# Revit family: 2060533 Sylvania Lighting Fixture ASCENT100 II ARCH 1900 3K DALI EMG 120
name_source: partatom
category: Lighting Fixtures
revit_build: Autodesk Revit 2016 (Build: 20150220_1215(x64)
units: mm (PartAtom-declared; Revit-internal decimal feet)

## family parameters
Cut with Voids When Loaded = No
Host = Face
Light Source = Yes
OmniClass Number = 23.80.70.11.17
OmniClass Title = Specialized Lighting by Location or Use
Part Type = Normal
Room Calculation Point = No
Round Connector Dimension = Use Diameter
Shared = No

## types (2) — shared parameters
Aperture_SYL = 120 mm
Assembly Code = D5020200
AssetType = Fixed
Color Filter = 16777215
CutoutDiameter_SYL = 137 mm  [stored 0.449475 ft]
Description = Direct LED retro fit for original LED 100 Arch (120) single CFL lamp offering Matching lumen levels and improved light distribution of original LED 100 CFL lamp equivalents Typically half the power consumption compared to CFL Up to 104lm/W 120mm aperture Architectural reflector accepts range of glass accessories from existing LED 100 Arch 120 offering HE, HO and VHO versions equivalent of single 1 x 13W, 1 x 18W, 1 x 26W Additional VVHO versions which offer the performance circa 2 x 26W equivalent
Diameter_SYL = 150 mm
DiffuserRadius_SYL = 53 mm  [stored 0.173885 ft]
Dimming Lamp Color Temperature Shift = <None>
DocumentationLiterature = http://www.sylvania-lighting.com
DurationUnit = hours
ElectricShockClassification = Class II
Emit Shape Visible in Rendering = No
Emit from Circle Diameter = 106 mm  [stored 0.347769 ft]
ExpectedLife = 50000
Height_SYL = 94 mm  [stored 0.308399 ft]
IfcExportAs = IfcLightFixtureType
IfcExportType = IfcLightFixtureType
ImpactProtectionIndex = IK02
IngressProtection = IP40
Keynote = 16500
Lamp = LED
LampColourRenderingIndex = 80
LampColourTemperature = 3000 K
LampNominalLuminous = 1887 lm
LampsType = LED
LightOutputRatio = 100
LuminousEfficacy = 94 lm/W
Manufacturer = Feilo Sylvania
ManufacturerName = Feilo Sylvania
Material = aluminium housing, acrylic diffuser
Material_1_SYL = Aluminum_Sylvania_Ascent_White
Material_2_SYL = Aluminum_Sylvania_Ascent_White
Material_3_SYL = Polycarbonate_Sylvania_Ascent_Clear
Material_4_SYL = Aluminium_Sylvania_Ascent_Silver
ModelNumber = 2060533
NominalHeight = 94 mm  [stored 0.308399 ft]
PowerConsumption = 20 W
Radius_SYL = 75 mm
ReflectorRadius_SYL = 60 mm  [stored 0.19685 ft]
Tilt Angle = -90°
URL = http://www.sylvania-lighting.com
Voltage = 0 V
Weight = 1.43 kg
zero-valued in all types: Default Elevation, NominalLength, NominalWidth, PowerFactor

## per-type parameters (varying)
| type | Apparent Load | Model | ModelReference | Name | Photometric Web File | TypeName |
| 2060533 ASCT100 II ARCH 1900 3K DALI EMG 120 Emergency mode | 2 VA | ASCT100 II ARCH 1900 3K DALI EMG 120 Emergency mode | ASCT100 II ARCH 1900 3K DALI EMG 120 Emergency mode | ASCT100 II ARCH 1900 3K DALI EMG 120 Emergency mode | 2060533EM.ies | ASCT100 II ARCH 1900 3K DALI EMG 120 Emergency mode |
| 2060533 ASCT100 II ARCH 1900 3K DALI EMG 120 | 20 VA | ASCENT100 II ARCH 1900 3K DALI EMG 120 | ASCENT100 II ARCH 1900 3K DALI EMG 120 | ASCENT100 II ARCH 1900 3K DALI EMG 120 | 2060533.ies | ASCENT100 II ARCH 1900 3K DALI EMG 120 |

note: [stored X ft] marks values corroborated as IEEE doubles in the binary element streams (Revit-internal decimal feet)

## geometry (parser evidence)
native form markers: Sweep x3
no freeform markers — native parametric forms only
